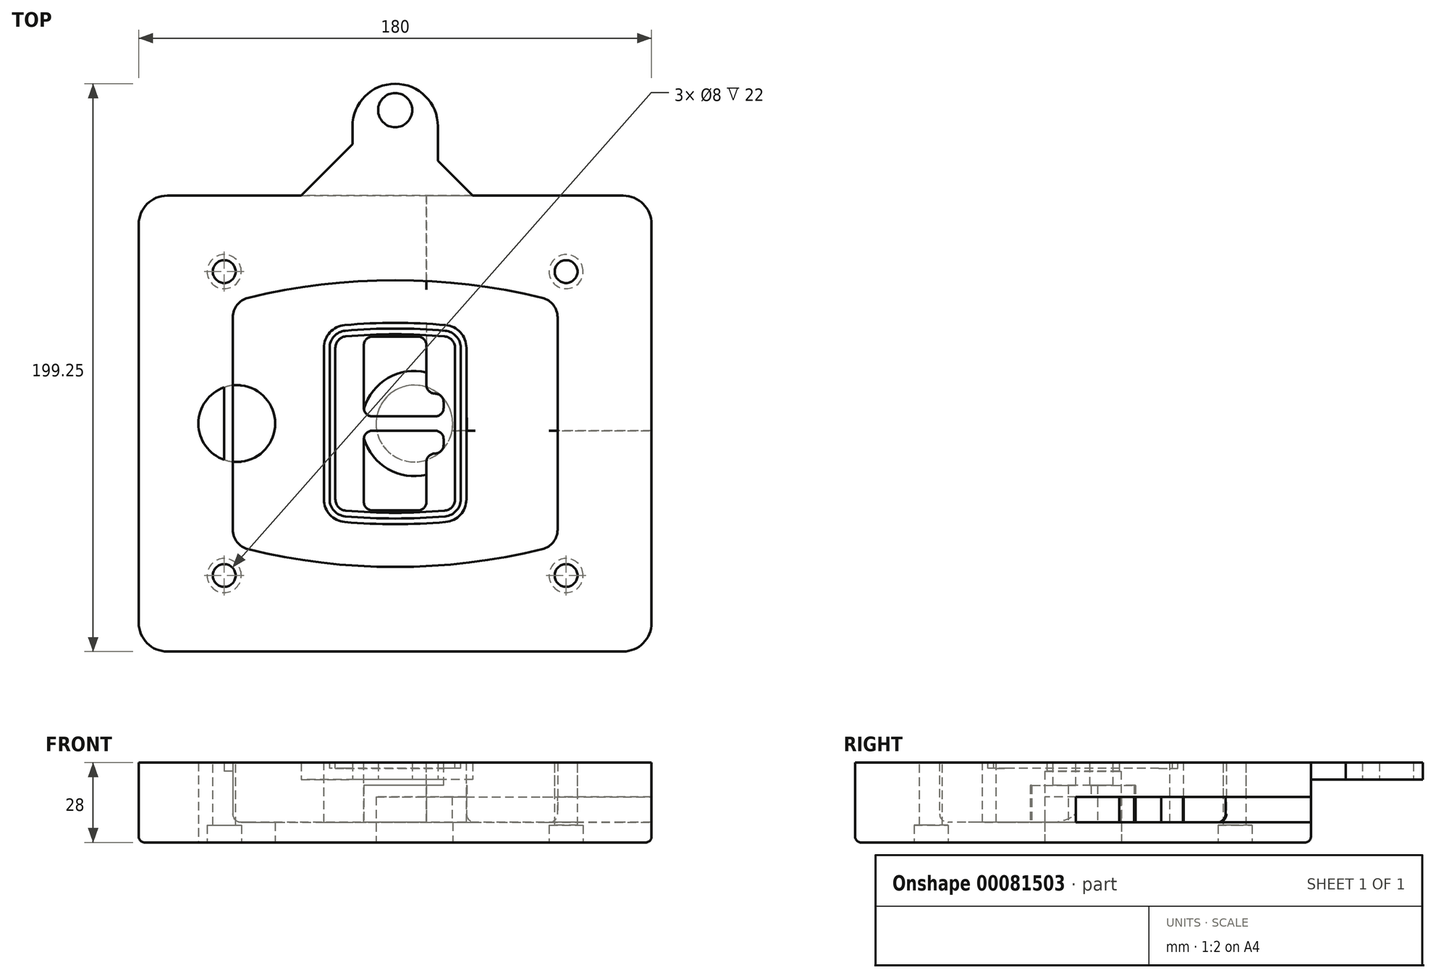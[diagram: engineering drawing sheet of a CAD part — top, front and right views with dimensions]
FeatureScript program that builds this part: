
annotation { "Feature Type Name" : "Feature", "Feature Type Description" : "" }
export const myFeature = defineFeature(function(context is Context, id is Id, definition is map)
    precondition{}
    {
        {
            var Q0;
            Q0=qCreatedBy(makeId("Top.planeOp"),FACE);
            var sketch = newSketch(context, id + "F0", { "sketchPlane" : qUnion([Q0])});
            skPoint(sketch, "E0.rect.middle", {"position": v(0, 0) * mm});
            skLineSegment(sketch, "E1.bottom", {"start": v(-80, -80) * mm, "end": v(80, -80) * mm});
            skLineSegment(sketch, "E1.top", {"start": v(-80, 80) * mm, "end": v(80, 80) * mm});
            skLineSegment(sketch, "E1.left", {"start": v(-90, -70) * mm, "end": v(-90, 70) * mm});
            skLineSegment(sketch, "E1.right", {"start": v(90, -70) * mm, "end": v(90, 70) * mm});
            skLineSegment(sketch, "E2", {"start": v(-90, 80) * mm, "end": v(90, -80) * mm, "construction": true});
            skLineSegment(sketch, "E3", {"start": v(90, 80) * mm, "end": v(-90, -80) * mm, "construction": true});
            skCircle(sketch, "E4", {"center": v(-60, 53.33) * mm, "radius": 4 * mm});
            skCircle(sketch, "E5", {"center": v(60, 53.33) * mm, "radius": 4 * mm});
            skCircle(sketch, "E6", {"center": v(60, -53.33) * mm, "radius": 4 * mm});
            skCircle(sketch, "E7", {"center": v(-60, -53.33) * mm, "radius": 4 * mm});
            skLineSegment(sketch, "E8", {"start": v(-60, 53.33) * mm, "end": v(60, 53.33) * mm, "construction": true});
            skLineSegment(sketch, "E9", {"start": v(60, 53.33) * mm, "end": v(60, -53.33) * mm, "construction": true});
            skLineSegment(sketch, "E10", {"start": v(60, -53.33) * mm, "end": v(-60, -53.33) * mm, "construction": true});
            skLineSegment(sketch, "E11", {"start": v(-60, -53.33) * mm, "end": v(-60, 53.33) * mm, "construction": true});
            skLineSegment(sketch, "E12", {"start": v(-60, 37.3) * mm, "end": v(-60, -37.3) * mm});
            skLineSegment(sketch, "E13", {"start": v(60, 37.3) * mm, "end": v(60, -37.3) * mm});
            skArc(sketch, "E14", {"start": v(52.38, 47.01) * mm, "mid": v(0, 53.33) * mm, "end": v(-52.38, 47.01) * mm});
            skArc(sketch, "E15", {"start": v(-52.38, -47.01) * mm, "mid": v(0, -53.33) * mm, "end": v(52.38, -47.01) * mm});
            skLineSegment(sketch, "E16", {"start": v(-60, 0) * mm, "end": v(60, 0) * mm, "construction": true});
            skPoint(sketch, "E17.visualSharp", {"position": v(-60, -45) * mm});
            skArc(sketch, "E17.filletArc", {"start": v(-60, -37.3) * mm, "mid": v(-57.87, -43.47) * mm, "end": v(-52.38, -47.01) * mm});
            skPoint(sketch, "E18.visualSharp", {"position": v(-60, 45) * mm});
            skArc(sketch, "E18.filletArc", {"start": v(-52.38, 47.01) * mm, "mid": v(-57.87, 43.47) * mm, "end": v(-60, 37.3) * mm});
            skPoint(sketch, "E19.visualSharp", {"position": v(60, 45) * mm});
            skArc(sketch, "E19.filletArc", {"start": v(60, 37.3) * mm, "mid": v(57.87, 43.47) * mm, "end": v(52.38, 47.01) * mm});
            skPoint(sketch, "E20.visualSharp", {"position": v(60, -45) * mm});
            skArc(sketch, "E20.filletArc", {"start": v(52.38, -47.01) * mm, "mid": v(57.87, -43.47) * mm, "end": v(60, -37.3) * mm});
            skPoint(sketch, "E21.visualSharp", {"position": v(-90, 80) * mm});
            skArc(sketch, "E21.filletArc", {"start": v(-80, 80) * mm, "mid": v(-87.07, 77.07) * mm, "end": v(-90, 70) * mm});
            skPoint(sketch, "E22.visualSharp", {"position": v(90, 80) * mm});
            skArc(sketch, "E22.filletArc", {"start": v(90, 70) * mm, "mid": v(87.07, 77.07) * mm, "end": v(80, 80) * mm});
            skPoint(sketch, "E23.visualSharp", {"position": v(90, -80) * mm});
            skArc(sketch, "E23.filletArc", {"start": v(80, -80) * mm, "mid": v(87.07, -77.07) * mm, "end": v(90, -70) * mm});
            skPoint(sketch, "E24.visualSharp", {"position": v(-90, -80) * mm});
            skArc(sketch, "E24.filletArc", {"start": v(-90, -70) * mm, "mid": v(-87.07, -77.07) * mm, "end": v(-80, -80) * mm});
            skArc(sketch, "E25.0", {"start": v(57, 37.3) * mm, "mid": v(55.5, 41.62) * mm, "end": v(51.67, 44.1) * mm});
            skLineSegment(sketch, "E25.1", {"start": v(57, 37.3) * mm, "end": v(57, -37.3) * mm});
            skArc(sketch, "E25.2", {"start": v(51.67, -44.1) * mm, "mid": v(55.5, -41.62) * mm, "end": v(57, -37.3) * mm});
            skArc(sketch, "E25.3", {"start": v(-51.67, -44.1) * mm, "mid": v(0, -50.33) * mm, "end": v(51.67, -44.1) * mm});
            skArc(sketch, "E25.4", {"start": v(-57, -37.3) * mm, "mid": v(-55.5, -41.62) * mm, "end": v(-51.67, -44.1) * mm});
            skArc(sketch, "E25.5", {"start": v(51.67, 44.1) * mm, "mid": v(0, 50.33) * mm, "end": v(-51.67, 44.1) * mm});
            skLineSegment(sketch, "E25.6", {"start": v(-57, 37.3) * mm, "end": v(-57, -37.3) * mm});
            skArc(sketch, "E25.7", {"start": v(-51.67, 44.1) * mm, "mid": v(-55.5, 41.62) * mm, "end": v(-57, 37.3) * mm});
            skArc(sketch, "E26.0", {"start": v(-53.33, 50.9) * mm, "mid": v(-61.01, 45.94) * mm, "end": v(-64, 37.3) * mm});
            skArc(sketch, "E26.1", {"start": v(53.33, 50.9) * mm, "mid": v(0, 57.33) * mm, "end": v(-53.33, 50.9) * mm});
            skArc(sketch, "E26.2", {"start": v(64, 37.3) * mm, "mid": v(61.01, 45.94) * mm, "end": v(53.33, 50.9) * mm});
            skLineSegment(sketch, "E26.3", {"start": v(64, 37.3) * mm, "end": v(64, -37.3) * mm});
            skArc(sketch, "E26.4", {"start": v(53.33, -50.9) * mm, "mid": v(61.01, -45.94) * mm, "end": v(64, -37.3) * mm});
            skLineSegment(sketch, "E26.5", {"start": v(-64, 37.3) * mm, "end": v(-64, -37.3) * mm});
            skArc(sketch, "E26.6", {"start": v(-53.33, -50.9) * mm, "mid": v(0, -57.33) * mm, "end": v(53.33, -50.9) * mm});
            skArc(sketch, "E26.7", {"start": v(-64, -37.3) * mm, "mid": v(-61.01, -45.94) * mm, "end": v(-53.33, -50.9) * mm});
            skSolve(sketch);
        }
        {
            var Q0;
            Q0=makeQuery(id+"F0.imprint","IMPRINT",FACE,{"disambiguationData":[TD([[makeQuery(id+"F0.imprint","IMPRINT",EDGE,{"derivedFrom":sQuery(id+"F0.wireOp",EDGE,"E1.bottom")}),1.0]])]});
            var Q1;
            Q1=makeQuery(id+"F0.imprint","IMPRINT",FACE,{"disambiguationData":[TD([[makeQuery(id+"F0.imprint","IMPRINT",EDGE,{"derivedFrom":sQuery(id+"F0.wireOp",EDGE,"E12")}),1.0]])]});
            var Q2;
            Q2=makeQuery(id+"F0.imprint","IMPRINT",FACE,{"disambiguationData":[TD([[makeQuery(id+"F0.imprint","IMPRINT",EDGE,{"derivedFrom":sQuery(id+"F0.wireOp",EDGE,"E25.0")}),1.0]])]});
            var Q3;
            Q3=makeQuery(id+"F0.imprint","IMPRINT",FACE,{"disambiguationData":[TD([[makeQuery(id+"F0.imprint","IMPRINT",EDGE,{"derivedFrom":sQuery(id+"F0.wireOp",EDGE,"E12")}),-1.0]])]});
            extrude(context, id + "F1", {"entities" : qUnion([Q0, Q1, Q2, Q3]), "oppositeDirection" : true, "depth" : 25 * mm});
        }
        {
            var Q0;
            Q0=makeQuery(id+"F0.imprint","IMPRINT",FACE,{"disambiguationData":[TD([[makeQuery(id+"F0.imprint","IMPRINT",EDGE,{"derivedFrom":sQuery(id+"F0.wireOp",EDGE,"E12")}),1.0]])]});
            extrude(context, id + "F2", {"entities" : qUnion([Q0]), "operationType" : NewBodyOperationType.ADD, "depth" : 3 * mm});
        }
        {
            var Q0;
            Q0=makeQuery(id+"F0.imprint","IMPRINT",FACE,{"disambiguationData":[TD([[makeQuery(id+"F0.imprint","IMPRINT",EDGE,{"derivedFrom":sQuery(id+"F0.wireOp",EDGE,"E25.0")}),1.0]])]});
            extrude(context, id + "F3", {"entities" : qUnion([Q0]), "operationType" : NewBodyOperationType.REMOVE, "oppositeDirection" : true, "depth" : 18 * mm});
        }
        {
            var Q0;
            Q0=makeQuery(id+"F2.opExtrude","CAP_FACE",FACE,{"disambiguationData":[OSD([sQuery(id+"F0.wireOp",EDGE,"E12"),sQuery(id+"F0.wireOp",EDGE,"E13"),sQuery(id+"F0.wireOp",EDGE,"E14"),sQuery(id+"F0.wireOp",EDGE,"E15"),sQuery(id+"F0.wireOp",EDGE,"E17.filletArc"),sQuery(id+"F0.wireOp",EDGE,"E18.filletArc"),sQuery(id+"F0.wireOp",EDGE,"E19.filletArc"),sQuery(id+"F0.wireOp",EDGE,"E20.filletArc"),sQuery(id+"F0.wireOp",EDGE,"E25.0"),sQuery(id+"F0.wireOp",EDGE,"E25.1"),sQuery(id+"F0.wireOp",EDGE,"E25.2"),sQuery(id+"F0.wireOp",EDGE,"E25.3"),sQuery(id+"F0.wireOp",EDGE,"E25.4"),sQuery(id+"F0.wireOp",EDGE,"E25.5"),sQuery(id+"F0.wireOp",EDGE,"E25.6"),sQuery(id+"F0.wireOp",EDGE,"E25.7")])],"isStart":false});
            var sketch = newSketch(context, id + "F4", { "sketchPlane" : qUnion([Q0])});
            skArc(sketch, "E27.0", {"start": v(-17.7, -34.56) * mm, "mid": v(0, -35.33) * mm, "end": v(17.7, -34.56) * mm});
            skArc(sketch, "E28.0", {"start": v(17.7, 34.56) * mm, "mid": v(0, 35.33) * mm, "end": v(-17.7, 34.56) * mm});
            skLineSegment(sketch, "E29", {"start": v(-25, 26.59) * mm, "end": v(-25, -26.59) * mm});
            skLineSegment(sketch, "E30", {"start": v(25, 26.59) * mm, "end": v(25, -26.59) * mm});
            skLineSegment(sketch, "E31", {"start": v(-25, 33.78) * mm, "end": v(25, 33.78) * mm, "construction": true});
            skLineSegment(sketch, "E32", {"start": v(-25, -33.78) * mm, "end": v(25, -33.78) * mm, "construction": true});
            skPoint(sketch, "E33.visualSharp", {"position": v(-25, 33.78) * mm});
            skArc(sketch, "E33.filletArc", {"start": v(-17.7, 34.56) * mm, "mid": v(-22.9, 32) * mm, "end": v(-25, 26.59) * mm});
            skPoint(sketch, "E34.visualSharp", {"position": v(25, 33.78) * mm});
            skArc(sketch, "E34.filletArc", {"start": v(25, 26.59) * mm, "mid": v(22.9, 32) * mm, "end": v(17.7, 34.56) * mm});
            skPoint(sketch, "E35.visualSharp", {"position": v(25, -33.78) * mm});
            skArc(sketch, "E35.filletArc", {"start": v(17.7, -34.56) * mm, "mid": v(22.9, -32) * mm, "end": v(25, -26.59) * mm});
            skPoint(sketch, "E36.visualSharp", {"position": v(-25, -33.78) * mm});
            skArc(sketch, "E36.filletArc", {"start": v(-25, -26.59) * mm, "mid": v(-22.9, -32) * mm, "end": v(-17.7, -34.56) * mm});
            skArc(sketch, "E37.0", {"start": v(51.67, 44.1) * mm, "mid": v(0, 50.33) * mm, "end": v(-51.67, 44.1) * mm});
            skArc(sketch, "E37.1", {"start": v(-51.67, 44.1) * mm, "mid": v(-55.5, 41.62) * mm, "end": v(-57, 37.3) * mm});
            skLineSegment(sketch, "E37.2", {"start": v(-57, 37.3) * mm, "end": v(-57, -37.3) * mm});
            skArc(sketch, "E37.3", {"start": v(-57, -37.3) * mm, "mid": v(-55.5, -41.62) * mm, "end": v(-51.67, -44.1) * mm});
            skArc(sketch, "E37.4", {"start": v(-51.67, -44.1) * mm, "mid": v(0, -50.33) * mm, "end": v(51.67, -44.1) * mm});
            skArc(sketch, "E37.5", {"start": v(51.67, -44.1) * mm, "mid": v(55.5, -41.62) * mm, "end": v(57, -37.3) * mm});
            skLineSegment(sketch, "E37.6", {"start": v(57, 37.3) * mm, "end": v(57, -37.3) * mm});
            skArc(sketch, "E37.7", {"start": v(57, 37.3) * mm, "mid": v(55.5, 41.62) * mm, "end": v(51.67, 44.1) * mm});
            skLineSegment(sketch, "E38.0", {"start": v(23, 26.59) * mm, "end": v(23, -26.59) * mm});
            skArc(sketch, "E38.1", {"start": v(17.53, -32.56) * mm, "mid": v(21.42, -30.64) * mm, "end": v(23, -26.59) * mm});
            skArc(sketch, "E38.2", {"start": v(-17.53, -32.56) * mm, "mid": v(0, -33.33) * mm, "end": v(17.53, -32.56) * mm});
            skArc(sketch, "E38.3", {"start": v(-23, -26.59) * mm, "mid": v(-21.42, -30.64) * mm, "end": v(-17.53, -32.56) * mm});
            skLineSegment(sketch, "E38.4", {"start": v(-23, 26.59) * mm, "end": v(-23, -26.59) * mm});
            skArc(sketch, "E38.5", {"start": v(23, 26.59) * mm, "mid": v(21.42, 30.64) * mm, "end": v(17.53, 32.56) * mm});
            skArc(sketch, "E38.6", {"start": v(-17.53, 32.56) * mm, "mid": v(-21.42, 30.64) * mm, "end": v(-23, 26.59) * mm});
            skArc(sketch, "E38.7", {"start": v(17.53, 32.56) * mm, "mid": v(0, 33.33) * mm, "end": v(-17.53, 32.56) * mm});
            skArc(sketch, "E39.0", {"start": v(21, 26.59) * mm, "mid": v(19.95, 29.29) * mm, "end": v(17.35, 30.57) * mm});
            skLineSegment(sketch, "E39.1", {"start": v(21, 26.59) * mm, "end": v(21, -26.59) * mm});
            skArc(sketch, "E39.2", {"start": v(17.35, -30.57) * mm, "mid": v(19.95, -29.29) * mm, "end": v(21, -26.59) * mm});
            skArc(sketch, "E39.3", {"start": v(-17.35, -30.57) * mm, "mid": v(0, -31.33) * mm, "end": v(17.35, -30.57) * mm});
            skArc(sketch, "E39.4", {"start": v(-21, -26.59) * mm, "mid": v(-19.95, -29.29) * mm, "end": v(-17.35, -30.57) * mm});
            skArc(sketch, "E39.5", {"start": v(17.35, 30.57) * mm, "mid": v(0, 31.33) * mm, "end": v(-17.35, 30.57) * mm});
            skLineSegment(sketch, "E39.6", {"start": v(-21, 26.59) * mm, "end": v(-21, -26.59) * mm});
            skArc(sketch, "E39.7", {"start": v(-17.35, 30.57) * mm, "mid": v(-19.95, 29.29) * mm, "end": v(-21, 26.59) * mm});
            skLineSegment(sketch, "E40", {"start": v(-25, 0) * mm, "end": v(25, 0) * mm, "construction": true});
            skLineSegment(sketch, "E41", {"start": v(-11, 5.5) * mm, "end": v(-11, 27.5) * mm});
            skLineSegment(sketch, "E42", {"start": v(-8, 30.5) * mm, "end": v(8, 30.5) * mm});
            skLineSegment(sketch, "E43", {"start": v(11, 27.5) * mm, "end": v(11, 13.5) * mm});
            skLineSegment(sketch, "E44", {"start": v(14, 10.5) * mm, "end": v(14, 10.5) * mm});
            skLineSegment(sketch, "E45", {"start": v(17, 7.5) * mm, "end": v(17, 5.5) * mm});
            skLineSegment(sketch, "E46", {"start": v(14, 2.5) * mm, "end": v(-8, 2.5) * mm});
            skPoint(sketch, "E47.visualSharp", {"position": v(-11, 30.5) * mm});
            skArc(sketch, "E47.filletArc", {"start": v(-8, 30.5) * mm, "mid": v(-10.12, 29.62) * mm, "end": v(-11, 27.5) * mm});
            skPoint(sketch, "E48.visualSharp", {"position": v(11, 30.5) * mm});
            skArc(sketch, "E48.filletArc", {"start": v(11, 27.5) * mm, "mid": v(10.12, 29.62) * mm, "end": v(8, 30.5) * mm});
            skPoint(sketch, "E49.visualSharp", {"position": v(11, 10.5) * mm});
            skArc(sketch, "E49.filletArc", {"start": v(11, 13.5) * mm, "mid": v(11.88, 11.38) * mm, "end": v(14, 10.5) * mm});
            skPoint(sketch, "E50.visualSharp", {"position": v(17, 10.5) * mm});
            skArc(sketch, "E50.filletArc", {"start": v(17, 7.5) * mm, "mid": v(16.12, 9.62) * mm, "end": v(14, 10.5) * mm});
            skPoint(sketch, "E51.visualSharp", {"position": v(17, 2.5) * mm});
            skArc(sketch, "E51.filletArc", {"start": v(14, 2.5) * mm, "mid": v(16.12, 3.38) * mm, "end": v(17, 5.5) * mm});
            skPoint(sketch, "E52.visualSharp", {"position": v(-11, 2.5) * mm});
            skArc(sketch, "E52.filletArc", {"start": v(-11, 5.5) * mm, "mid": v(-10.12, 3.38) * mm, "end": v(-8, 2.5) * mm});
            skLineSegment(sketch, "E53.0.MirrorCS", {"start": v(14, -2.5) * mm, "end": v(-8, -2.5) * mm});
            skArc(sketch, "E54.0.MirrorCS", {"start": v(-11, -5.5) * mm, "mid": v(-10.12, -3.38) * mm, "end": v(-8, -2.5) * mm});
            skLineSegment(sketch, "E55.0.MirrorCS", {"start": v(-11, -5.5) * mm, "end": v(-11, -27.5) * mm});
            skArc(sketch, "E56.0.MirrorCS", {"start": v(-8, -30.5) * mm, "mid": v(-10.12, -29.62) * mm, "end": v(-11, -27.5) * mm});
            skLineSegment(sketch, "E57.0.MirrorCS", {"start": v(-8, -30.5) * mm, "end": v(8, -30.5) * mm});
            skArc(sketch, "E58.0.MirrorCS", {"start": v(11, -27.5) * mm, "mid": v(10.12, -29.62) * mm, "end": v(8, -30.5) * mm});
            skLineSegment(sketch, "E59.0.MirrorCS", {"start": v(11, -27.5) * mm, "end": v(11, -13.5) * mm});
            skArc(sketch, "E60.0.MirrorCS", {"start": v(11, -13.5) * mm, "mid": v(11.88, -11.38) * mm, "end": v(14, -10.5) * mm});
            skArc(sketch, "E61.0.MirrorCS", {"start": v(17, -7.5) * mm, "mid": v(16.12, -9.62) * mm, "end": v(14, -10.5) * mm});
            skLineSegment(sketch, "E62.0.MirrorCS", {"start": v(17, -7.5) * mm, "end": v(17, -5.5) * mm});
            skArc(sketch, "E63.0.MirrorCS", {"start": v(14, -2.5) * mm, "mid": v(16.12, -3.38) * mm, "end": v(17, -5.5) * mm});
            skSolve(sketch);
        }
        {
            var Q0;
            Q0=makeQuery(id+"F4.imprint","IMPRINT",FACE,{"disambiguationData":[TD([[makeQuery(id+"F4.imprint","IMPRINT",EDGE,{"derivedFrom":sQuery(id+"F4.wireOp",EDGE,"E27.0")}),1.0]])]});
            var Q1;
            Q1=makeQuery(id+"F4.imprint","IMPRINT",FACE,{"disambiguationData":[TD([[makeQuery(id+"F4.imprint","IMPRINT",EDGE,{"derivedFrom":sQuery(id+"F4.wireOp",EDGE,"E38.0")}),-1.0]])]});
            var Q2;
            Q2=makeQuery(id+"F4.imprint","IMPRINT",FACE,{"disambiguationData":[TD([[makeQuery(id+"F4.imprint","IMPRINT",EDGE,{"derivedFrom":sQuery(id+"F4.wireOp",EDGE,"E39.0")}),1.0]])]});
            extrude(context, id + "F5", {"entities" : qUnion([Q0, Q1, Q2]), "operationType" : NewBodyOperationType.ADD, "endBound" : BoundingType.UP_TO_NEXT, "oppositeDirection" : true, "depth" : 25 * mm});
        }
        {
            var Q0;
            Q0=makeQuery(id+"F4.imprint","IMPRINT",FACE,{"disambiguationData":[TD([[makeQuery(id+"F4.imprint","IMPRINT",EDGE,{"derivedFrom":sQuery(id+"F4.wireOp",EDGE,"E38.0")}),-1.0]])]});
            extrude(context, id + "F6", {"entities" : qUnion([Q0]), "operationType" : NewBodyOperationType.REMOVE, "oppositeDirection" : true, "depth" : 2 * mm});
        }
        {
            var Q0;
            Q0=makeQuery(id+"F1.opExtrude","CAP_FACE",FACE,{"disambiguationData":[OSD([sQuery(id+"F0.wireOp",EDGE,"E1.bottom"),sQuery(id+"F0.wireOp",EDGE,"E1.top"),sQuery(id+"F0.wireOp",EDGE,"E1.left"),sQuery(id+"F0.wireOp",EDGE,"E1.right"),sQuery(id+"F0.wireOp",EDGE,"E4"),sQuery(id+"F0.wireOp",EDGE,"E5"),sQuery(id+"F0.wireOp",EDGE,"E6"),sQuery(id+"F0.wireOp",EDGE,"E7"),sQuery(id+"F0.wireOp",EDGE,"E21.filletArc"),sQuery(id+"F0.wireOp",EDGE,"E22.filletArc"),sQuery(id+"F0.wireOp",EDGE,"E23.filletArc"),sQuery(id+"F0.wireOp",EDGE,"E24.filletArc")])],"isStart":false});
            var sketch = newSketch(context, id + "F7", { "sketchPlane" : qUnion([Q0])});
            skCircle(sketch, "E64", {"center": v(6.76, 0) * mm, "radius": 13.47 * mm});
            skCircle(sketch, "E65", {"center": v(-55.56, 0) * mm, "radius": 13.47 * mm});
            skLineSegment(sketch, "E66", {"start": v(90, 0) * mm, "end": v(-90, 0) * mm});
            skCircle(sketch, "E67", {"center": v(6.76, 0) * mm, "radius": 18.47 * mm});
            skCircle(sketch, "E68", {"center": v(60, -53.33) * mm, "radius": 6 * mm});
            skCircle(sketch, "E69", {"center": v(-60, -53.33) * mm, "radius": 6 * mm});
            skCircle(sketch, "E70", {"center": v(-60, 53.33) * mm, "radius": 6 * mm});
            skCircle(sketch, "E71", {"center": v(60, 53.33) * mm, "radius": 6 * mm});
            skSolve(sketch);
        }
        {
            var Q0;
            {var subQ1=sQuery(id+"F7.wireOp",EDGE,"E66");var subQ4=sQuery(id+"F7.wireOp",EDGE,"E64");var subQ6=makeQuery(id+"F7.imprint","INTERSECT",VERTEX,{"disambiguationData":[OD(0.0)],"derivedFrom":[subQ4,subQ1]});Q0=makeQuery(id+"F7.imprint","IMPRINT",FACE,{"disambiguationData":[TD([[makeQuery(id+"F7.imprint","IMPRINT",EDGE,{"disambiguationData":[TD([[subQ6,-1.0]])],"derivedFrom":subQ4}),-1.0]])]});}
            var Q1;
            {var subQ0=sQuery(id+"F7.wireOp",EDGE,"E66");var subQ1=sQuery(id+"F7.wireOp",EDGE,"E64");var subQ3=makeQuery(id+"F7.imprint","INTERSECT",VERTEX,{"disambiguationData":[OD(0.0)],"derivedFrom":[subQ1,subQ0]});Q1=makeQuery(id+"F7.imprint","IMPRINT",FACE,{"disambiguationData":[TD([[makeQuery(id+"F7.imprint","IMPRINT",EDGE,{"disambiguationData":[TD([[subQ3,-1.0]])],"derivedFrom":subQ1}),1.0]])]});}
            var Q2;
            {var subQ0=sQuery(id+"F7.wireOp",EDGE,"E66");var subQ1=sQuery(id+"F7.wireOp",EDGE,"E64");var subQ3=makeQuery(id+"F7.imprint","INTERSECT",VERTEX,{"disambiguationData":[OD(0.0)],"derivedFrom":[subQ1,subQ0]});Q2=makeQuery(id+"F7.imprint","IMPRINT",FACE,{"disambiguationData":[TD([[makeQuery(id+"F7.imprint","IMPRINT",EDGE,{"disambiguationData":[TD([[subQ3,1.0]])],"derivedFrom":subQ1}),1.0]])]});}
            var Q3;
            {var subQ1=sQuery(id+"F7.wireOp",EDGE,"E66");var subQ4=sQuery(id+"F7.wireOp",EDGE,"E64");var subQ6=makeQuery(id+"F7.imprint","INTERSECT",VERTEX,{"disambiguationData":[OD(0.0)],"derivedFrom":[subQ4,subQ1]});Q3=makeQuery(id+"F7.imprint","IMPRINT",FACE,{"disambiguationData":[TD([[makeQuery(id+"F7.imprint","IMPRINT",EDGE,{"disambiguationData":[TD([[subQ6,1.0]])],"derivedFrom":subQ4}),-1.0]])]});}
            extrude(context, id + "F8", {"entities" : qUnion([Q0, Q1, Q2, Q3]), "operationType" : NewBodyOperationType.ADD, "oppositeDirection" : true, "depth" : 20 * mm});
        }
        {
            var Q0;
            {var subQ0=sQuery(id+"F7.wireOp",EDGE,"E66");var subQ1=sQuery(id+"F7.wireOp",EDGE,"E64");var subQ3=makeQuery(id+"F7.imprint","INTERSECT",VERTEX,{"disambiguationData":[OD(0.0)],"derivedFrom":[subQ1,subQ0]});Q0=makeQuery(id+"F7.imprint","IMPRINT",FACE,{"disambiguationData":[TD([[makeQuery(id+"F7.imprint","IMPRINT",EDGE,{"disambiguationData":[TD([[subQ3,-1.0]])],"derivedFrom":subQ1}),1.0]])]});}
            var Q1;
            {var subQ0=sQuery(id+"F7.wireOp",EDGE,"E66");var subQ1=sQuery(id+"F7.wireOp",EDGE,"E64");var subQ3=makeQuery(id+"F7.imprint","INTERSECT",VERTEX,{"disambiguationData":[OD(0.0)],"derivedFrom":[subQ1,subQ0]});Q1=makeQuery(id+"F7.imprint","IMPRINT",FACE,{"disambiguationData":[TD([[makeQuery(id+"F7.imprint","IMPRINT",EDGE,{"disambiguationData":[TD([[subQ3,1.0]])],"derivedFrom":subQ1}),1.0]])]});}
            extrude(context, id + "F9", {"entities" : qUnion([Q0, Q1]), "operationType" : NewBodyOperationType.REMOVE, "oppositeDirection" : true, "depth" : 16 * mm});
        }
        {
            var Q0;
            {var subQ0=sQuery(id+"F7.wireOp",EDGE,"E66");var subQ1=sQuery(id+"F7.wireOp",EDGE,"E65");var subQ3=makeQuery(id+"F7.imprint","INTERSECT",VERTEX,{"disambiguationData":[OD(0.0)],"derivedFrom":[subQ1,subQ0]});Q0=makeQuery(id+"F7.imprint","IMPRINT",FACE,{"disambiguationData":[TD([[makeQuery(id+"F7.imprint","IMPRINT",EDGE,{"disambiguationData":[TD([[subQ3,-1.0]])],"derivedFrom":subQ1}),1.0]])]});}
            var Q1;
            {var subQ0=sQuery(id+"F7.wireOp",EDGE,"E66");var subQ1=sQuery(id+"F7.wireOp",EDGE,"E65");var subQ3=makeQuery(id+"F7.imprint","INTERSECT",VERTEX,{"disambiguationData":[OD(0.0)],"derivedFrom":[subQ1,subQ0]});Q1=makeQuery(id+"F7.imprint","IMPRINT",FACE,{"disambiguationData":[TD([[makeQuery(id+"F7.imprint","IMPRINT",EDGE,{"disambiguationData":[TD([[subQ3,1.0]])],"derivedFrom":subQ1}),1.0]])]});}
            extrude(context, id + "F10", {"entities" : qUnion([Q0, Q1]), "operationType" : NewBodyOperationType.REMOVE, "oppositeDirection" : true, "depth" : 25 * mm});
        }
        {
            var Q0;
            Q0=makeQuery(id+"F7.imprint","IMPRINT",FACE,{"disambiguationData":[TD([[makeQuery(id+"F7.imprint","IMPRINT",EDGE,{"derivedFrom":sQuery(id+"F7.wireOp",EDGE,"E68")}),1.0]])]});
            var Q1;
            Q1=makeQuery(id+"F7.imprint","IMPRINT",FACE,{"disambiguationData":[TD([[makeQuery(id+"F7.imprint","IMPRINT",EDGE,{"derivedFrom":makeQuery(id+"F1.opExtrude","CAP_EDGE",EDGE,{"disambiguationData":[OSD([sQuery(id+"F0.wireOp",EDGE,"E5")])],"isStart":false})}),-1.0]])]});
            var Q2;
            Q2=makeQuery(id+"F7.imprint","IMPRINT",FACE,{"disambiguationData":[TD([[makeQuery(id+"F7.imprint","IMPRINT",EDGE,{"derivedFrom":sQuery(id+"F7.wireOp",EDGE,"E69")}),1.0]])]});
            var Q3;
            Q3=makeQuery(id+"F7.imprint","IMPRINT",FACE,{"disambiguationData":[TD([[makeQuery(id+"F7.imprint","IMPRINT",EDGE,{"derivedFrom":makeQuery(id+"F1.opExtrude","CAP_EDGE",EDGE,{"disambiguationData":[OSD([sQuery(id+"F0.wireOp",EDGE,"E4")])],"isStart":false})}),-1.0]])]});
            var Q4;
            Q4=makeQuery(id+"F7.imprint","IMPRINT",FACE,{"disambiguationData":[TD([[makeQuery(id+"F7.imprint","IMPRINT",EDGE,{"derivedFrom":sQuery(id+"F7.wireOp",EDGE,"E70")}),1.0]])]});
            var Q5;
            Q5=makeQuery(id+"F7.imprint","IMPRINT",FACE,{"disambiguationData":[TD([[makeQuery(id+"F7.imprint","IMPRINT",EDGE,{"derivedFrom":makeQuery(id+"F1.opExtrude","CAP_EDGE",EDGE,{"disambiguationData":[OSD([sQuery(id+"F0.wireOp",EDGE,"E7")])],"isStart":false})}),-1.0]])]});
            var Q6;
            Q6=makeQuery(id+"F7.imprint","IMPRINT",FACE,{"disambiguationData":[TD([[makeQuery(id+"F7.imprint","IMPRINT",EDGE,{"derivedFrom":sQuery(id+"F7.wireOp",EDGE,"E71")}),1.0]])]});
            var Q7;
            Q7=makeQuery(id+"F7.imprint","IMPRINT",FACE,{"disambiguationData":[TD([[makeQuery(id+"F7.imprint","IMPRINT",EDGE,{"derivedFrom":makeQuery(id+"F1.opExtrude","CAP_EDGE",EDGE,{"disambiguationData":[OSD([sQuery(id+"F0.wireOp",EDGE,"E6")])],"isStart":false})}),-1.0]])]});
            extrude(context, id + "F11", {"entities" : qUnion([Q0, Q1, Q2, Q3, Q4, Q5, Q6, Q7]), "operationType" : NewBodyOperationType.REMOVE, "oppositeDirection" : true, "depth" : 6 * mm});
        }
        {
            var Q0;
            Q0=makeQuery(id+"F9.boolean.opBoolean","COPY",FACE,{"derivedFrom":makeQuery(id+"F9.opExtrude","CAP_FACE",FACE,{"disambiguationData":[OSD([sQuery(id+"F7.wireOp",EDGE,"E64")])],"isStart":false})});
            var sketch = newSketch(context, id + "F12", { "sketchPlane" : qUnion([Q0])});
            skArc(sketch, "E72.0", {"start": v(11, -88.19) * mm, "mid": v(97.1, -83.6) * mm, "end": v(92.5, 2.5) * mm});
            skLineSegment(sketch, "E72.1", {"start": v(11, -17.97) * mm, "end": v(11, -17.97) * mm});
            skLineSegment(sketch, "E73", {"start": v(92.5, -105.13) * mm, "end": v(102.3, -105.13) * mm});
            skLineSegment(sketch, "E74.0", {"start": v(92.5, 2.5) * mm, "end": v(14, 2.5) * mm});
            skArc(sketch, "E74.1", {"start": v(14, 2.5) * mm, "mid": v(16.12, 3.38) * mm, "end": v(17, 5.5) * mm});
            skLineSegment(sketch, "E74.2", {"start": v(17, 7.5) * mm, "end": v(17, 5.5) * mm});
            skArc(sketch, "E74.3", {"start": v(17, 7.5) * mm, "mid": v(16.12, 9.62) * mm, "end": v(14, 10.5) * mm});
            skArc(sketch, "E74.4", {"start": v(11, 13.5) * mm, "mid": v(11.88, 11.38) * mm, "end": v(14, 10.5) * mm});
            skLineSegment(sketch, "E74.5", {"start": v(11, 13.5) * mm, "end": v(11, -88.19) * mm});
            skLineSegment(sketch, "E74.7", {"start": v(92.5, -2.5) * mm, "end": v(14, -2.5) * mm});
            skArc(sketch, "E74.8", {"start": v(14, -2.5) * mm, "mid": v(16.12, -3.38) * mm, "end": v(17, -5.5) * mm});
            skLineSegment(sketch, "E74.9", {"start": v(17, -7.5) * mm, "end": v(17, -5.5) * mm});
            skArc(sketch, "E74.10", {"start": v(17, -7.5) * mm, "mid": v(16.12, -9.62) * mm, "end": v(14, -10.5) * mm});
            skArc(sketch, "E74.11", {"start": v(11, -13.5) * mm, "mid": v(11.88, -11.38) * mm, "end": v(14, -10.5) * mm});
            skLineSegment(sketch, "E74.12", {"start": v(11, -17.97) * mm, "end": v(11, -13.5) * mm});
            skPoint(sketch, "E75.orphan", {"position": v(11, -27.5) * mm});
            skPoint(sketch, "E76.orphan", {"position": v(-8, -2.5) * mm});
            skPoint(sketch, "E77.orphan", {"position": v(-8, 2.5) * mm});
            skPoint(sketch, "E78.orphan", {"position": v(11, 27.5) * mm});
            skSolve(sketch);
        }
        {
            var Q0;
            {var subQ7=sQuery(id+"F12.wireOp",EDGE,"E72.0");var subQ14=sQuery(id+"F12.wireOp",EDGE,"E72.1");var subQ16=sQuery(id+"F12.wireOp",EDGE,"E74.1");var subQ18=sQuery(id+"F12.wireOp",EDGE,"E74.8");Q0=qUnion([makeQuery(id+"F12.imprint","IMPRINT",FACE,{"disambiguationData":[TD([[makeQuery(id+"F12.imprint","IMPRINT",EDGE,{"derivedFrom":subQ7}),1.0]])]}),makeQuery(id+"F12.imprint","IMPRINT",FACE,{"disambiguationData":[TD([[makeQuery(id+"F12.imprint","IMPRINT",EDGE,{"derivedFrom":subQ14}),1.0]])]}),makeQuery(id+"F12.imprint","IMPRINT",FACE,{"disambiguationData":[TD([[makeQuery(id+"F12.imprint","IMPRINT",EDGE,{"derivedFrom":subQ16}),1.0]])]}),makeQuery(id+"F12.imprint","IMPRINT",FACE,{"disambiguationData":[TD([[makeQuery(id+"F12.imprint","IMPRINT",EDGE,{"derivedFrom":subQ18}),-1.0]])]})]);}
            var Q1;
            Q1=makeQuery(id+"F5.boolean.opBoolean","SPLIT",FACE,{"disambiguationData":[TD([makeQuery(id+"F5.opExtrude","SWEPT_FACE",FACE,{"disambiguationData":[OSD([sQuery(id+"F4.wireOp",EDGE,"E41")])]})])],"derivedFrom":makeQuery(id+"F3.boolean.opBoolean","COPY",FACE,{"derivedFrom":makeQuery(id+"F3.opExtrude","CAP_FACE",FACE,{"disambiguationData":[OSD([sQuery(id+"F0.wireOp",EDGE,"E25.0"),sQuery(id+"F0.wireOp",EDGE,"E25.1"),sQuery(id+"F0.wireOp",EDGE,"E25.2"),sQuery(id+"F0.wireOp",EDGE,"E25.3"),sQuery(id+"F0.wireOp",EDGE,"E25.4"),sQuery(id+"F0.wireOp",EDGE,"E25.5"),sQuery(id+"F0.wireOp",EDGE,"E25.6"),sQuery(id+"F0.wireOp",EDGE,"E25.7")])],"isStart":false})})});
            extrude(context, id + "F13", {"entities" : qUnion([Q0]), "operationType" : NewBodyOperationType.REMOVE, "endBound" : BoundingType.UP_TO_SURFACE, "endBoundEntityFace" : qUnion([Q1]), "depth" : 25 * mm});
        }
        {
            var Q0;
            Q0=makeQuery(id+"F3.boolean.opBoolean","COPY",EDGE,{"derivedFrom":makeQuery(id+"F3.opExtrude","CAP_EDGE",EDGE,{"disambiguationData":[OSD([sQuery(id+"F0.wireOp",EDGE,"E25.6")])],"isStart":false})});
            var Q1;
            Q1=makeQuery(id+"F8.boolean.opBoolean","INTERSECT",EDGE,{"derivedFrom":[makeQuery(id+"F5.opExtrude","SWEPT_FACE",FACE,{"disambiguationData":[OSD([sQuery(id+"F4.wireOp",EDGE,"E30")])]}),makeQuery(id+"F8.opExtrude","CAP_FACE",FACE,{"disambiguationData":[OSD([sQuery(id+"F7.wireOp",EDGE,"E67")])],"isStart":false})]});
            var Q2;
            Q2=makeQuery(id+"F8.boolean.opBoolean","INTERSECT",EDGE,{"disambiguationData":[OD(1.0)],"derivedFrom":[makeQuery(id+"F5.opExtrude","SWEPT_FACE",FACE,{"disambiguationData":[OSD([sQuery(id+"F4.wireOp",EDGE,"E30")])]}),makeQuery(id+"F8.opExtrude","SWEPT_FACE",FACE,{"disambiguationData":[OSD([sQuery(id+"F7.wireOp",EDGE,"E67")])]})]});
            var Q3;
            {var subQ0=makeQuery(id+"F3.boolean.opBoolean","COPY",FACE,{"derivedFrom":makeQuery(id+"F3.opExtrude","CAP_FACE",FACE,{"disambiguationData":[OSD([sQuery(id+"F0.wireOp",EDGE,"E25.0"),sQuery(id+"F0.wireOp",EDGE,"E25.1"),sQuery(id+"F0.wireOp",EDGE,"E25.2"),sQuery(id+"F0.wireOp",EDGE,"E25.3"),sQuery(id+"F0.wireOp",EDGE,"E25.4"),sQuery(id+"F0.wireOp",EDGE,"E25.5"),sQuery(id+"F0.wireOp",EDGE,"E25.6"),sQuery(id+"F0.wireOp",EDGE,"E25.7")])],"isStart":false})});var subQ1=sQuery(id+"F4.wireOp",EDGE,"E30");Q3=makeQuery(id+"F8.boolean.opBoolean","SPLIT",EDGE,{"disambiguationData":[TD([makeQuery(id+"F5.opExtrude","SWEPT_FACE",FACE,{"disambiguationData":[OSD([sQuery(id+"F4.wireOp",EDGE,"E35.filletArc")])]})])],"derivedFrom":makeQuery(id+"F5.opExtrude","TWEAK_EDGE",EDGE,{"derivedFrom":[subQ0,makeQuery(id+"F4.imprint","IMPRINT",EDGE,{"derivedFrom":subQ1})]})});}
            var Q4;
            {var subQ0=sQuery(id+"F0.wireOp",EDGE,"E25.0");var subQ1=sQuery(id+"F0.wireOp",EDGE,"E25.1");var subQ2=sQuery(id+"F0.wireOp",EDGE,"E25.2");var subQ3=sQuery(id+"F0.wireOp",EDGE,"E25.3");var subQ4=sQuery(id+"F0.wireOp",EDGE,"E25.4");var subQ5=sQuery(id+"F0.wireOp",EDGE,"E25.5");var subQ6=sQuery(id+"F0.wireOp",EDGE,"E25.6");var subQ7=sQuery(id+"F0.wireOp",EDGE,"E25.7");Q4=makeQuery(id+"F8.boolean.opBoolean","INTERSECT",EDGE,{"derivedFrom":[makeQuery(id+"F5.boolean.opBoolean","SPLIT",FACE,{"disambiguationData":[TD([makeQuery(id+"F2.opExtrude","SWEPT_FACE",FACE,{"disambiguationData":[OSD([subQ0])]})])],"derivedFrom":makeQuery(id+"F3.boolean.opBoolean","COPY",FACE,{"derivedFrom":makeQuery(id+"F3.opExtrude","CAP_FACE",FACE,{"disambiguationData":[OSD([subQ0,subQ1,subQ2,subQ3,subQ4,subQ5,subQ6,subQ7])],"isStart":false})})}),makeQuery(id+"F8.opExtrude","SWEPT_FACE",FACE,{"disambiguationData":[OSD([sQuery(id+"F7.wireOp",EDGE,"E67")])]})]});}
            var Q5;
            Q5=makeQuery(id+"F8.boolean.opBoolean","INTERSECT",EDGE,{"disambiguationData":[OD(0.0)],"derivedFrom":[makeQuery(id+"F5.opExtrude","SWEPT_FACE",FACE,{"disambiguationData":[OSD([sQuery(id+"F4.wireOp",EDGE,"E30")])]}),makeQuery(id+"F8.opExtrude","SWEPT_FACE",FACE,{"disambiguationData":[OSD([sQuery(id+"F7.wireOp",EDGE,"E67")])]})]});
            fillet(context, id + "F14", {"entities" : qUnion([Q0, Q1, Q2, Q3, Q4, Q5]), "radius" : 3 * mm, "tangentPropagation" : true, "allowEdgeOverflow" : false});
        }
        {
            var Q0;
            Q0=makeQuery(id+"F1.opExtrude","CAP_EDGE",EDGE,{"disambiguationData":[OSD([sQuery(id+"F0.wireOp",EDGE,"E1.bottom")])],"isStart":false});
            fillet(context, id + "F15", {"entities" : qUnion([Q0]), "radius" : 2 * mm, "tangentPropagation" : true, "allowEdgeOverflow" : false});
        }
        {
            var Q0;
            {var subQ0=sQuery(id+"F0.wireOp",EDGE,"E22.filletArc");var subQ1=sQuery(id+"F0.wireOp",EDGE,"E7");var subQ2=sQuery(id+"F0.wireOp",EDGE,"E6");var subQ3=sQuery(id+"F0.wireOp",EDGE,"E5");var subQ4=sQuery(id+"F0.wireOp",EDGE,"E4");var subQ5=sQuery(id+"F0.wireOp",EDGE,"E1.bottom");var subQ6=sQuery(id+"F0.wireOp",EDGE,"E21.filletArc");var subQ7=sQuery(id+"F0.wireOp",EDGE,"E1.top");var subQ8=sQuery(id+"F0.wireOp",EDGE,"E1.left");var subQ9=sQuery(id+"F0.wireOp",EDGE,"E1.right");var subQ10=sQuery(id+"F0.wireOp",EDGE,"E23.filletArc");var subQ11=sQuery(id+"F0.wireOp",EDGE,"E24.filletArc");Q0=makeQuery(id+"F2.boolean.opBoolean","SPLIT",FACE,{"disambiguationData":[TD([makeQuery(id+"F1.opExtrude","SWEPT_FACE",FACE,{"disambiguationData":[OSD([subQ5])]})])],"derivedFrom":makeQuery(id+"F1.opExtrude","CAP_FACE",FACE,{"disambiguationData":[OSD([subQ5,subQ7,subQ8,subQ9,subQ4,subQ3,subQ2,subQ1,subQ6,subQ0,subQ10,subQ11])],"isStart":true})});}
            var sketch = newSketch(context, id + "F16", { "sketchPlane" : qUnion([Q0])});
            skLineSegment(sketch, "E79.0", {"start": v(-80, 80) * mm, "end": v(80, 80) * mm});
            skArc(sketch, "E79.1", {"start": v(-80, 80) * mm, "mid": v(-87.07, 77.07) * mm, "end": v(-90, 70) * mm});
            skLineSegment(sketch, "E79.2", {"start": v(-90, -70) * mm, "end": v(-90, 70) * mm});
            skArc(sketch, "E79.3", {"start": v(90, 70) * mm, "mid": v(87.07, 77.07) * mm, "end": v(80, 80) * mm});
            skLineSegment(sketch, "E79.4", {"start": v(90, -70) * mm, "end": v(90, 70) * mm});
            skArc(sketch, "E79.5", {"start": v(80, -80) * mm, "mid": v(87.07, -77.07) * mm, "end": v(90, -70) * mm});
            skLineSegment(sketch, "E79.6", {"start": v(-80, -80) * mm, "end": v(80, -80) * mm});
            skArc(sketch, "E79.7", {"start": v(-90, -70) * mm, "mid": v(-87.07, -77.07) * mm, "end": v(-80, -80) * mm});
            skCircle(sketch, "E79.8", {"center": v(-60, -53.33) * mm, "radius": 4 * mm});
            skCircle(sketch, "E79.9", {"center": v(-60, 53.33) * mm, "radius": 4 * mm});
            skCircle(sketch, "E79.10", {"center": v(60, 53.33) * mm, "radius": 4 * mm});
            skCircle(sketch, "E79.11", {"center": v(60, -53.33) * mm, "radius": 4 * mm});
            skArc(sketch, "E79.12", {"start": v(52.38, -47.01) * mm, "mid": v(57.87, -43.47) * mm, "end": v(60, -37.3) * mm});
            skLineSegment(sketch, "E79.13", {"start": v(60, 37.3) * mm, "end": v(60, -37.3) * mm});
            skArc(sketch, "E79.14", {"start": v(-52.38, -47.01) * mm, "mid": v(0, -53.33) * mm, "end": v(52.38, -47.01) * mm});
            skArc(sketch, "E79.15", {"start": v(-60, -37.3) * mm, "mid": v(-57.87, -43.47) * mm, "end": v(-52.38, -47.01) * mm});
            skLineSegment(sketch, "E79.16", {"start": v(-60, 37.3) * mm, "end": v(-60, -37.3) * mm});
            skArc(sketch, "E79.17", {"start": v(-52.38, 47.01) * mm, "mid": v(-57.87, 43.47) * mm, "end": v(-60, 37.3) * mm});
            skArc(sketch, "E79.18", {"start": v(52.38, 47.01) * mm, "mid": v(0, 53.33) * mm, "end": v(-52.38, 47.01) * mm});
            skArc(sketch, "E79.19", {"start": v(60, 37.3) * mm, "mid": v(57.87, 43.47) * mm, "end": v(52.38, 47.01) * mm});
            skPoint(sketch, "E80.endSnap0", {"position": v(0, 80) * mm});
            skLineSegment(sketch, "E81", {"start": v(0, 80) * mm, "end": v(0, 110) * mm, "construction": true});
            skCircle(sketch, "E82", {"center": v(0, 110) * mm, "radius": 6 * mm});
            skLineSegment(sketch, "E83", {"start": v(-33, 80) * mm, "end": v(-15, 98) * mm});
            skLineSegment(sketch, "E84", {"start": v(-15, 98) * mm, "end": v(-15, 104.25) * mm});
            skLineSegment(sketch, "E85", {"start": v(27.25, 80) * mm, "end": v(15, 92.25) * mm});
            skLineSegment(sketch, "E86", {"start": v(15, 92.25) * mm, "end": v(15, 104.25) * mm});
            skArc(sketch, "E87", {"start": v(15, 104.25) * mm, "mid": v(0, 119.25) * mm, "end": v(-15, 104.25) * mm});
            skLineSegment(sketch, "E88", {"start": v(-90, 0) * mm, "end": v(90, 0) * mm, "construction": true});
            skArc(sketch, "E89.MirrorCS", {"start": v(15, -104.25) * mm, "mid": v(0, -119.25) * mm, "end": v(-15, -104.25) * mm});
            skLineSegment(sketch, "E90.MirrorCS", {"start": v(-15, -98) * mm, "end": v(-15, -104.25) * mm});
            skLineSegment(sketch, "E91.MirrorCS", {"start": v(-33, -80) * mm, "end": v(-15, -98) * mm});
            skLineSegment(sketch, "E92.MirrorCS", {"start": v(27.25, -80) * mm, "end": v(15, -92.25) * mm});
            skCircle(sketch, "E93.MirrorC", {"center": v(0, -110) * mm, "radius": 6 * mm});
            skLineSegment(sketch, "E94.MirrorCS", {"start": v(15, -92.25) * mm, "end": v(15, -104.25) * mm});
            skLineSegment(sketch, "E95.MirrorCS", {"start": v(0, -80) * mm, "end": v(0, -110) * mm, "construction": true});
            skSolve(sketch);
        }
        {
            var Q0;
            Q0=makeQuery(id+"F16.imprint","IMPRINT",FACE,{"disambiguationData":[TD([[makeQuery(id+"F16.imprint","IMPRINT",EDGE,{"derivedFrom":sQuery(id+"F16.wireOp",EDGE,"E82")}),-1.0]])]});
            var Q1;
            {var subQ4=sQuery(id+"F16.wireOp",EDGE,"E79.1");Q1=makeQuery(id+"F16.imprint","IMPRINT",FACE,{"disambiguationData":[TD([[makeQuery(id+"F16.imprint","IMPRINT",EDGE,{"derivedFrom":subQ4}),1.0]])]});}
            var Q2;
            Q2=makeQuery(id+"F16.imprint","IMPRINT",FACE,{"disambiguationData":[TD([[makeQuery(id+"F16.imprint","IMPRINT",EDGE,{"derivedFrom":sQuery(id+"F16.wireOp",EDGE,"E89.MirrorCS")}),-1.0]])]});
            extrude(context, id + "F17", {"entities" : qUnion([Q0, Q1, Q2]), "operationType" : NewBodyOperationType.ADD, "endBound" : BoundingType.SYMMETRIC, "depth" : 6 * mm});
        }
    });
